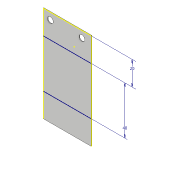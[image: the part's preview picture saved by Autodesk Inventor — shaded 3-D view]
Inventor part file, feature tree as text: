
AUTODESK INVENTOR PART (.ipt)
format: ipt  version: 2019 (Build 230136000, 136)  size: 100,352 bytes
history: native  units: mm
features: sketch x4, sheet_metal_op x1, hole x1, other x1
ambient origin geometry x8: Origin, YZ Plane, XZ Plane, XY Plane, X Axis, Y Axis, Z Axis, Center Point
bodies: Solid1 (feature_tree)
feature tree (7):
  sheet_metal_op  "Face1"
  sketch  "Sketch6"  dims[d2=0.5mm]
  sketch  "Sketch7"  dims[d10=20.0mm]
  hole  "Hole3"  [1 undecoded]
  sketch  "Sketch1"  dims[d0=40.0mm d1=80.0mm]
  other  "Plate1"
  sketch  "Sketch10"  dims[d11=40.0mm d20=4.82mm d21=6.0mm d22=4.0mm d23=2.0mm d24=90.0deg d25=0.5mm d26=20.594885mm d13=1.0mm d14=1.0mm d15=1.0mm d16=0.15mm d17=0.25mm d18=0.375mm d19=14.3117mm d27=0.75mm d28=20.594885mm d29=0.0625mm d30=0.75mm d31=0.375mm]
note: 1 required parameter value undecoded (feature->parameter linkage not recoverable at this tier; creation-order binding heuristic only, values carry confidence <= 0.55)
